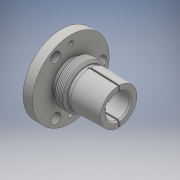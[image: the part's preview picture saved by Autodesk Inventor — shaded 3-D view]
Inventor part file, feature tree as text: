
AUTODESK INVENTOR PART (.ipt)
format: ipt  version: 2016 (Build 200138000, 138)  size: 273,920 bytes
history: native  units: mm
features: sketch x5, extrude x3, hole x2, pattern_circular x2, revolve x1, chamfer x1, thread x1, plane x1
ambient origin geometry x8: Origin, YZ Plane, XZ Plane, XY Plane, X Axis, Y Axis, Z Axis, Center Point
bodies: Solid1 (feature_tree)
feature tree (16):
  revolve  "Revolution1"  [1 undecoded]
  hole  "Hole1"  [1 undecoded]
  pattern_circular  "Circular Pattern1"  [2 undecoded]
  hole  "Hole2"  [1 undecoded]
  pattern_circular  "Circular Pattern2"  Angle=60.0deg  [1 undecoded]
  extrude  "Extrusion1"  Depth=8.0mm
  extrude  "Extrusion2"  TaperAngle=60.0deg  [1 undecoded]
  chamfer  "Chamfer1"  Distance=0.901924mm
  thread  "Thread1"  [1 undecoded]
  plane  "Work Plane1"
  extrude  "Extrusion3"  Depth=8.0mm
  sketch  "Sketch2"  dims[d0=60.0mm d1=12.5mm]
  sketch  "Sketch3"  dims[d2=27.5mm d3=10.0mm]
  sketch  "Sketch4"  dims[d4=21.0mm]
  sketch  "Sketch5"  dims[d5=4.0mm]
  sketch  "Sketch6"  dims[d9=4.0mm d11=1.0mm d20=1.5mm d21=60.0deg d22=1.5mm d23=60.0deg d25=0.901924mm d26=0.901924mm d28=60.0mm d29=0.349066mm d30=7.5mm d31=9.0mm d32=2.5mm d33=40.0mm d34=90.0deg d35=10.5mm d36=6.0mm d37=4.0mm d38=2.0mm d39=90.0deg d40=8.0mm d41=20.594885mm d42=30.0mm d43=360.0deg d45=5.0mm d46=6.0mm d47=4.0mm d48=2.0mm d49=90.0deg d50=8.0mm d51=20.594885mm d52=20.0mm d53=360.0deg d55=1.5mm d56=0.75mm d57=32.0mm d58=0.0mm d59=53.0mm d60=120.0deg d61=6.0mm d62=15.5mm d63=32.0mm d64=0.0mm d65=1.5mm d66=2.0mm d67=45.0deg d68=10.0mm d69=0.0mm d70=17.5mm d71=8.0mm d72=38.0mm d73=50.0mm d74=26.5mm d75=0.0mm]
note: 8 required parameter values undecoded (feature->parameter linkage not recoverable at this tier; creation-order binding heuristic only, values carry confidence <= 0.55)